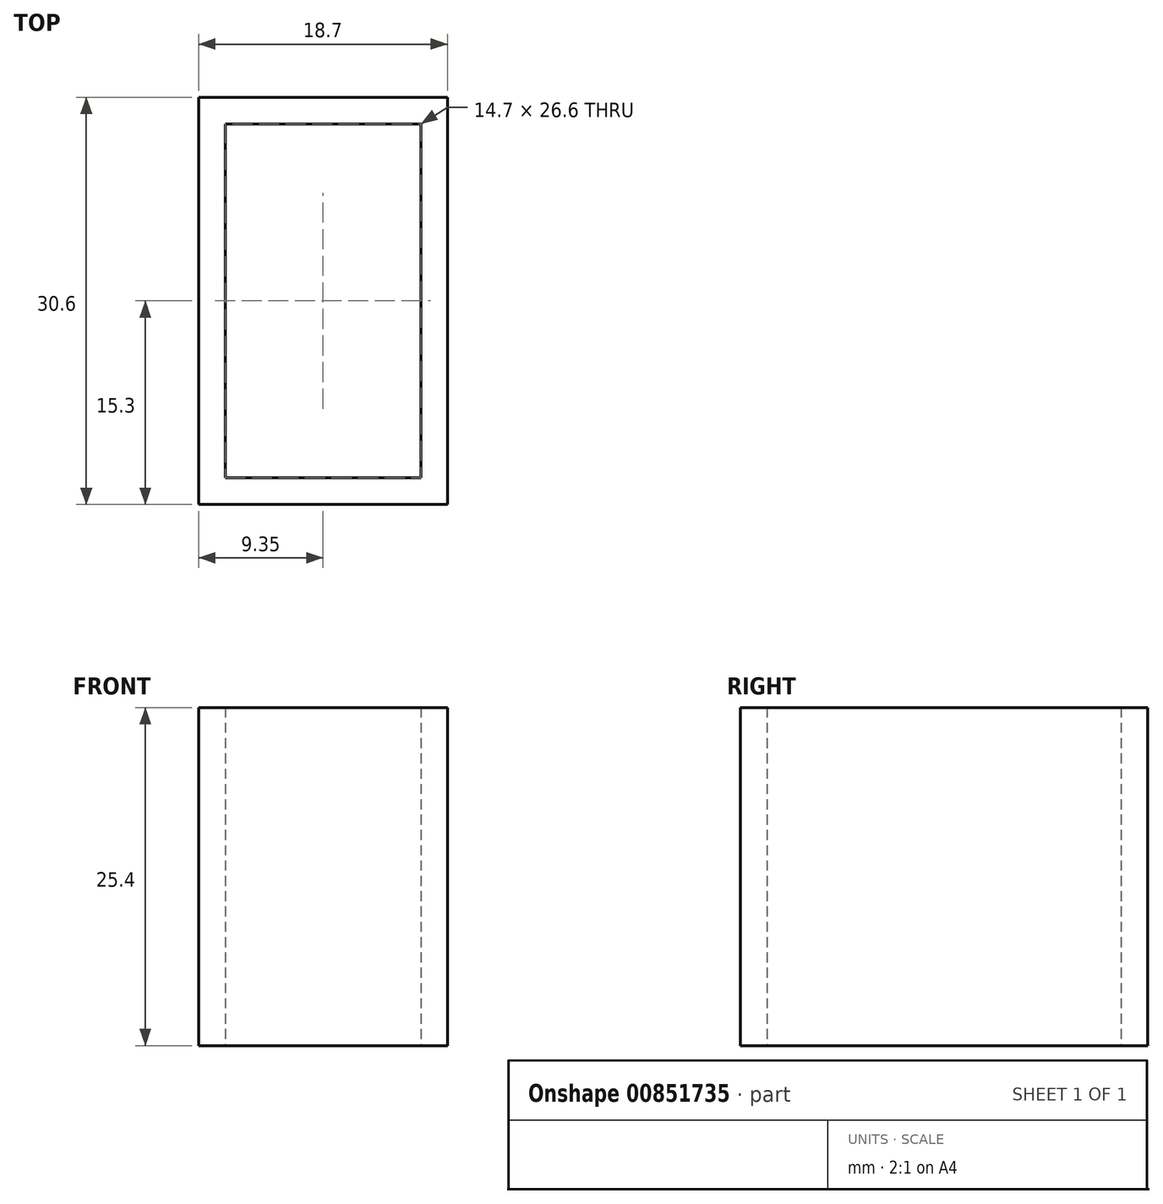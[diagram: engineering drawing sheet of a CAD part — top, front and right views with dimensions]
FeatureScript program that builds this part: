
annotation { "Feature Type Name" : "Feature", "Feature Type Description" : "" }
export const myFeature = defineFeature(function(context is Context, id is Id, definition is map)
    precondition{}
    {
        {
            var Q0;
            Q0=qCreatedBy(makeId("Top.planeOp"),FACE);
            var sketch = newSketch(context, id + "F0", { "sketchPlane" : qUnion([Q0])});
            skLineSegment(sketch, "E0.bottom", {"start": v(5.25, -9.5) * mm, "end": v(-5.25, -9.5) * mm});
            skLineSegment(sketch, "E0.top", {"start": v(5.25, 9.5) * mm, "end": v(-5.25, 9.5) * mm});
            skLineSegment(sketch, "E0.left", {"start": v(5.25, -9.5) * mm, "end": v(5.25, 9.5) * mm});
            skLineSegment(sketch, "E0.right", {"start": v(-5.25, -9.5) * mm, "end": v(-5.25, 9.5) * mm});
            skPoint(sketch, "E0.middle", {"position": v(0, 0) * mm});
            skLineSegment(sketch, "E1.bottom", {"start": v(7.35, -13.3) * mm, "end": v(-7.35, -13.3) * mm});
            skLineSegment(sketch, "E1.top", {"start": v(7.35, 13.3) * mm, "end": v(-7.35, 13.3) * mm});
            skLineSegment(sketch, "E1.left", {"start": v(7.35, -13.3) * mm, "end": v(7.35, 13.3) * mm});
            skLineSegment(sketch, "E1.right", {"start": v(-7.35, -13.3) * mm, "end": v(-7.35, 13.3) * mm});
            skLineSegment(sketch, "E2.bottom", {"start": v(9.35, -15.3) * mm, "end": v(-9.35, -15.3) * mm});
            skLineSegment(sketch, "E2.top", {"start": v(9.35, 15.3) * mm, "end": v(-9.35, 15.3) * mm});
            skLineSegment(sketch, "E2.left", {"start": v(9.35, -15.3) * mm, "end": v(9.35, 15.3) * mm});
            skLineSegment(sketch, "E2.right", {"start": v(-9.35, -15.3) * mm, "end": v(-9.35, 15.3) * mm});
            skSolve(sketch);
        }
        {
            var Q0;
            Q0=makeQuery(id+"F0.imprint","IMPRINT",FACE,{"disambiguationData":[TD([[makeQuery(id+"F0.imprint","IMPRINT",EDGE,{"derivedFrom":sQuery(id+"F0.wireOp",EDGE,"E1.bottom")}),1.0]])]});
            extrude(context, id + "F1", {"entities" : qUnion([Q0]), "depth" : 25 * mm, "offsetDistance" : 25.4 * mm});
        }
        {
            var Q0;
            Q0 = qSketchRegion(id + "F0", true);
            extrude(context, id + "F2", {"entities" : qUnion([Q0]), "operationType" : NewBodyOperationType.ADD, "depth" : 25.4 * mm, "offsetDistance" : 25.4 * mm});
        }
    });
